# Revit family: 2015_Ventana_Perfiles-Sapa_70mmRPT_2-Hojas-Corredera_X
name_source: partatom
category: Ventanas
revit_build: Autodesk Revit 2015 (Build: 20140606_1530(x64)
units: mm (PartAtom-declared; Revit-internal decimal feet)

## types (2) — shared parameters
Acristalamiento = Cristal - Vidrio claro templado
Altura = 1480 mm  [stored 4.85564 ft]
Altura Máxima = 2500 mm  [stored 8.2021 ft]
Altura Real = 1480 mm  [stored 4.85564 ft]
Altura de antepecho por defecto = 800 mm
AnchoMarco = 120.3 mm  [stored 0.394685 ft]
AnchoMarcoCentral = 80 mm  [stored 0.262467 ft]
Anchura = 1230 mm  [stored 4.03543 ft]
Anchura Máxima = 1800 mm  [stored 5.90551 ft]
Anchura Real = 1230 mm  [stored 4.03543 ft]
Area = 1820400 mm²
Autor = Bimetica Parametric Design Services, S.L.
Bimetica = http://www.bimetica.com
CerramientoExterior = Sí
Cierre de muro = Por anfitrión
CondicionesEvaluacion = *Transmitáncia térmica calculada para carpintería de 4,6 m² con vidrio bajo emisivo de altas prestaciones térmicas.
** Verntana de 1,23 x 1,48 m de dos hojas ( UNE-EN 14351-1:2006)
ConfiguracionPoliamidas = 280600 - 979400
ControlHumos = No
CosteEnergeticoMj = 0 J
Detalle Perfileria = Sí
Distancia Marco ventana a Guías persiana = 100 mm  [stored 0.328084 ft]
EstanqueidadAgua = Clase 8A (UNE-EN 1027:2000)
Fabricante = Perfiles de Sapa Extrusion
FactorSolarModificado = 3000000
FechaEmisionElementoBIM = 06/09/2016
FechaVencimientoElementoBIM = 06/09/2017
FraccionAreaAcristalamiento = 61.92%
GarantiaExtendida = No
GrosorAcristalamiento = 18 mm  [stored 0.0590551 ft]
GrosorMarco = 71 mm  [stored 0.23294 ft]
IndiceGlobalRedAcustica = Rw=30 dB ** (UNE-EN14351-1:2006)
Manija = Sí
Marco = Aluminio
MasterformatCodigo = 08 51 13
MasterformatTitulo = Aluminium Windows
Motorizada = No
NumeroSerie = C97R
OmniclassCodigo = 23.30.20.17.14.11
OmniclassTitulo = Vertical Sliding Window
Operación = Corredera
Oscilobatiente = No
Perimetro = 5420
PermeabilidadAlAire = Clase 3 (UNE-EN 1026:2000)
Poliamida = Poliamida, Technoform Bautec, PA66 GF 25
Practicable = Sí
Referencia = Perfil corredera RPT
ReferenciaContacto = Perfiles de Sapa Extrusion
RepisaExterior = Sí
RepisaInterior = No
ResistenciaAlViento = Clase C5 (UNE-EN 12210:2000)
SalidaEmergencia = No
TelefonoContacto = +34 947 02 73 00
Tirador = Aluminio
TransmitanciaTermica = 1.5 W/(m²·K)
UNSPSCCodigo = 30171600
UNSPSCTitulo = Windows
URL = http://www.sapagroup.es
URL Poliamida = http://www.technoform.es
URL Poliamida - Catálogo = http://www.technoform.com
URLProducto = http://www.sapagroup.es
Uniclass2.0Codigo = "25-30"
Uniclass2.0Titulo = "Door and window systems"
VersionElementoBIM = 1.0
Y𝑔 P1 = 0.47
Y𝑔 P2 = 0.47
a = 3184737.1768
𝐴𝑓 P1 = 594137.64
𝐴𝑓 P2 = 99152
𝐴𝑔 V1 = 563555.18
𝐴𝑔 V2 = 563555.18
𝑈𝑓 P1 = 2.42
𝑈𝑓 P2 = 3.039
𝑈𝑔 V1 = 1
𝑈𝑔 V2 = 1
𝑈𝑤 = 1.749471
𝑙𝑔 P1 = 4297.6
𝑙𝑔 P2 = 2478.8
zero-valued in all types: AcidificacionAtmosferica, AcidificacionAtmosfericaPorUnidad, AguaConsumida, AguaConsumidaPorUnidad, CambioClimatico, CambioClimaticoPorUnidad, CosteEnergeticoKwh, CosteMantenimiento, DestruccionCapaOzonoEstratosferica, DestruccionCapaOzonoEstratosfericaPorUnidad, EmisionCO2, EnergiaNoRenovableConsumida, EnergiaNoRenovableConsumidaPorUnidad, EnergiaPrimariaTotalConsumida, EnergiaPrimariaTotalConsumidaPorUnidad, EnergiaRenovableConsumida, EnergiaRenovableConsumidaPorUnidad, Eutrofizacion, EutrofizacionPorUnidad, FactorSombra, FaltaDeRecursos, FaltaDeRecursosPorUnidad, FormacionFotoquimicaOzono, FormacionFotoquimicaOzonoPorUnidad, MasaSuperficialKgm2, MateriaPrima, ResiduoInerte, ResiduoInertePorUnidad, ResiduoRadioactivo, ResiduoRadioactivoPorUnidad, ResiduosNoPeligrosos, ResiduosNoPeligrososPorUnidad, ResiduosPeligrosos, ResiduosPeligrososPorUnidad

## per-type parameters (varying)
| type | Ancho hueco con Monoblock | Comentarios de tipo | Descripción | Modelo | Monoblock |
| 1230 x 1480 - Corredera + Monoblock | 54.69 mm  [stored 0.179429 ft] | Sistema de Ventana de 2 Hojas Rotura de Puente Térmico Modelo Perfiles corredera 70mmRPT + Monoblock | Ventana Corredera + Monoblock | Perfiles corredera 70mmRPT + Monoblock | Sí |
| 1230 x 1480 - Corredera | 0 mm  [stored 0 ft] | Sistema de Ventana de 2 Hojas Rotura de Puente Térmico Modelo Perfiles corredera 70mmRPT | Ventana Corredera | Perfiles corredera 70mmRPT | No |

note: [stored X ft] marks values corroborated as IEEE doubles in the binary element streams (Revit-internal decimal feet)

## geometry (parser evidence)
native form markers: Blend x4, Extrusion x16
no freeform markers — native parametric forms only
